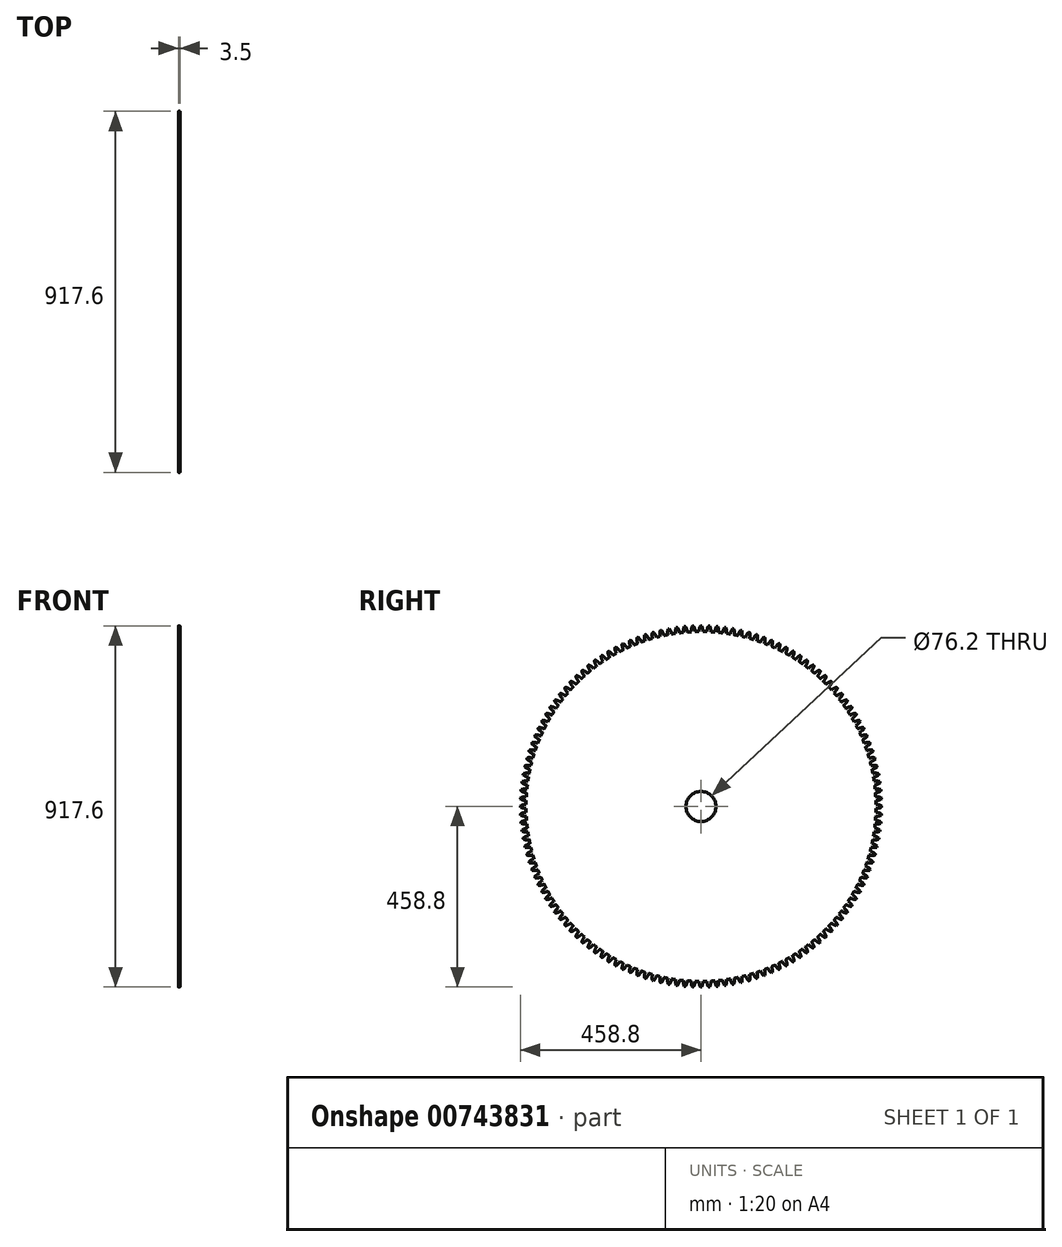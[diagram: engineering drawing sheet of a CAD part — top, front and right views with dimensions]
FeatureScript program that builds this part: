
annotation { "Feature Type Name" : "Feature", "Feature Type Description" : "" }
export const myFeature = defineFeature(function(context is Context, id is Id, definition is map)
    precondition{}
    {
        {
            assignVariable(context, id + "F0", {"name" : "FaceWidth", "anyValue" : 3.5});
        }
        {
            assignVariable(context, id + "F1", {"name" : "NumberTeeth", "anyValue" : 140});
        }
        {
            var Q0;
            Q0=qCreatedBy(makeId("Right.planeOp"),FACE);
            var sketch = newSketch(context, id + "F2", { "sketchPlane" : qUnion([Q0])});
            skCircle(sketch, "E0", {"center": v(0, 0) * mm, "radius": 444.5 * mm});
            skCircle(sketch, "E1", {"center": v(0, 0) * mm, "radius": 38.1 * mm});
            skCircle(sketch, "E2", {"center": v(0, 0) * mm, "radius": 452.45 * mm});
            skCircle(sketch, "E3", {"center": v(0, 0) * mm, "radius": 458.8 * mm});
            skPoint(sketch, "E4", {"position": v(0, 444.5) * mm});
            skPoint(sketch, "E5", {"position": v(0, 452.45) * mm});
            skPoint(sketch, "E6", {"position": v(0, 458.8) * mm});
            skLineSegment(sketch, "E7", {"start": v(-5.08, 458.77) * mm, "end": v(0, 0) * mm});
            skArc(sketch, "E8", {"start": v(-1.59, 458.8) * mm, "mid": v(-4.12, 451.84) * mm, "end": v(-4.93, 444.47) * mm});
            skPoint(sketch, "E9", {"position": v(-3.98, 452.43) * mm});
            skLineSegment(sketch, "E10", {"start": v(0, 458.8) * mm, "end": v(0, 444.5) * mm});
            skArc(sketch, "E11.MirrorCS", {"start": v(1.59, 458.8) * mm, "mid": v(4.12, 451.84) * mm, "end": v(4.93, 444.47) * mm});
            skLineSegment(sketch, "E12.MirrorCS", {"start": v(5.08, 458.77) * mm, "end": v(0, 0) * mm});
            skPoint(sketch, "E13", {"position": v(3.98, 452.43) * mm});
            skSolve(sketch);
        }
        {
            var Q0;
            {var subQ0=sQuery(id+"F2.wireOp",EDGE,"E7");var subQ5=sQuery(id+"F2.wireOp",EDGE,"E1");var subQ6=makeQuery(id+"F2.imprint","INTERSECT",VERTEX,{"derivedFrom":[subQ5,subQ0]});Q0=makeQuery(id+"F2.imprint","IMPRINT",FACE,{"disambiguationData":[TD([[makeQuery(id+"F2.imprint","IMPRINT",EDGE,{"disambiguationData":[TD([[subQ6,-1.0]])],"derivedFrom":subQ5}),-1.0]])]});}
            var Q1;
            {var subQ0=sQuery(id+"F2.wireOp",EDGE,"E7");var subQ3=sQuery(id+"F2.wireOp",EDGE,"E1");var subQ4=makeQuery(id+"F2.imprint","INTERSECT",VERTEX,{"derivedFrom":[subQ3,subQ0]});Q1=makeQuery(id+"F2.imprint","IMPRINT",FACE,{"disambiguationData":[TD([[makeQuery(id+"F2.imprint","IMPRINT",EDGE,{"disambiguationData":[TD([[subQ4,1.0]])],"derivedFrom":subQ3}),-1.0]])]});}
            extrude(context, id + "F3", {"entities" : qUnion([Q0, Q1]), "endBound" : BoundingType.SYMMETRIC, "depth" : (getVariable(context, 'FaceWidth')) * mm, "offsetDistance" : 25.4 * mm});
        }
        {
            var Q0;
            {var subQ0=sQuery(id+"F2.wireOp",EDGE,"E10");var subQ1=sQuery(id+"F2.wireOp",EDGE,"E2");var subQ2=makeQuery(id+"F2.imprint","INTERSECT",VERTEX,{"derivedFrom":[subQ1,subQ0]});Q0=makeQuery(id+"F2.imprint","IMPRINT",FACE,{"disambiguationData":[TD([[makeQuery(id+"F2.imprint","IMPRINT",EDGE,{"disambiguationData":[TD([[subQ2,-1.0]])],"derivedFrom":subQ1}),-1.0]])]});}
            var Q1;
            {var subQ0=sQuery(id+"F2.wireOp",EDGE,"E11.MirrorCS");var subQ1=sQuery(id+"F2.wireOp",EDGE,"E2");var subQ2=makeQuery(id+"F2.imprint","INTERSECT",VERTEX,{"derivedFrom":[subQ1,subQ0]});Q1=makeQuery(id+"F2.imprint","IMPRINT",FACE,{"disambiguationData":[TD([[makeQuery(id+"F2.imprint","IMPRINT",EDGE,{"disambiguationData":[TD([[subQ2,-1.0]])],"derivedFrom":subQ1}),-1.0]])]});}
            var Q2;
            {var subQ3=sQuery(id+"F2.wireOp",EDGE,"E11.MirrorCS");var subQ5=sQuery(id+"F2.wireOp",EDGE,"E2");var subQ6=makeQuery(id+"F2.imprint","INTERSECT",VERTEX,{"derivedFrom":[subQ5,subQ3]});Q2=makeQuery(id+"F2.imprint","IMPRINT",FACE,{"disambiguationData":[TD([[makeQuery(id+"F2.imprint","IMPRINT",EDGE,{"disambiguationData":[TD([[subQ6,-1.0]])],"derivedFrom":subQ5}),1.0]])]});}
            var Q3;
            {var subQ3=sQuery(id+"F2.wireOp",EDGE,"E10");var subQ5=sQuery(id+"F2.wireOp",EDGE,"E2");var subQ6=makeQuery(id+"F2.imprint","INTERSECT",VERTEX,{"derivedFrom":[subQ5,subQ3]});Q3=makeQuery(id+"F2.imprint","IMPRINT",FACE,{"disambiguationData":[TD([[makeQuery(id+"F2.imprint","IMPRINT",EDGE,{"disambiguationData":[TD([[subQ6,-1.0]])],"derivedFrom":subQ5}),1.0]])]});}
            extrude(context, id + "F4", {"entities" : qUnion([Q0, Q1, Q2, Q3]), "endBound" : BoundingType.SYMMETRIC, "depth" : (getVariable(context, 'FaceWidth')) * mm, "offsetDistance" : 25.4 * mm});
        }
        {
            var Q0;
            Q0=makeQuery(id+"F4.opExtrude","SWEPT_BODY",BODY,{"disambiguationData":[OSD([sQuery(id+"F2.wireOp",EDGE,"E0"),sQuery(id+"F2.wireOp",EDGE,"E3"),sQuery(id+"F2.wireOp",EDGE,"E8"),sQuery(id+"F2.wireOp",EDGE,"E11.MirrorCS")])]});
            var Q1;
            Q1=makeQuery(id+"F3.opExtrude","SWEPT_FACE",FACE,{"disambiguationData":[OSD([sQuery(id+"F2.wireOp",EDGE,"E1")])]});
            circularPattern(context, id + "F5", {"operationType" : NewBodyOperationType.ADD, "entities" : qUnion([Q0]), "axis" : qUnion([Q1]), "angle" : 360 * degree, "instanceCount" : getVariable(context, 'NumberTeeth'), "equalSpace" : true});
        }
    });
